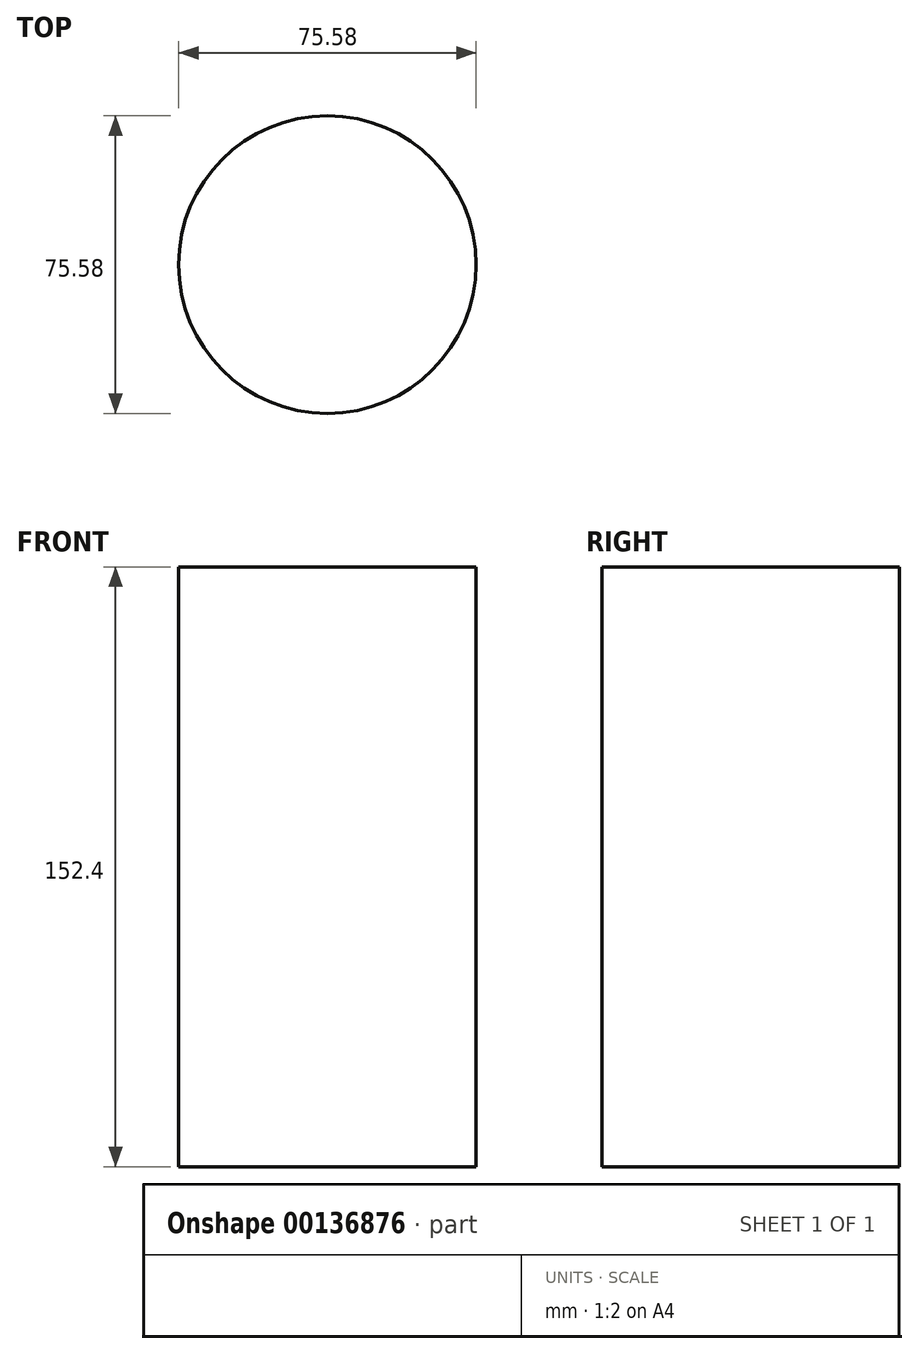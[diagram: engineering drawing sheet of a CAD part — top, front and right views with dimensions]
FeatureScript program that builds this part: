
annotation { "Feature Type Name" : "Feature", "Feature Type Description" : "" }
export const myFeature = defineFeature(function(context is Context, id is Id, definition is map)
    precondition{}
    {
        {
            var Q0;
            Q0=qCreatedBy(makeId("Top.planeOp"),FACE);
            var sketch = newSketch(context, id + "F0", { "sketchPlane" : qUnion([Q0])});
            skCircle(sketch, "E0", {"center": v(0, 0) * mm, "radius": 37.8 * mm});
            skSolve(sketch);
        }
        {
            var Q0;
            Q0 = qSketchRegion(id + "F0", true);
            extrude(context, id + "F1", {"entities" : qUnion([Q0]), "depth" : 152.4 * mm});
        }
    });
